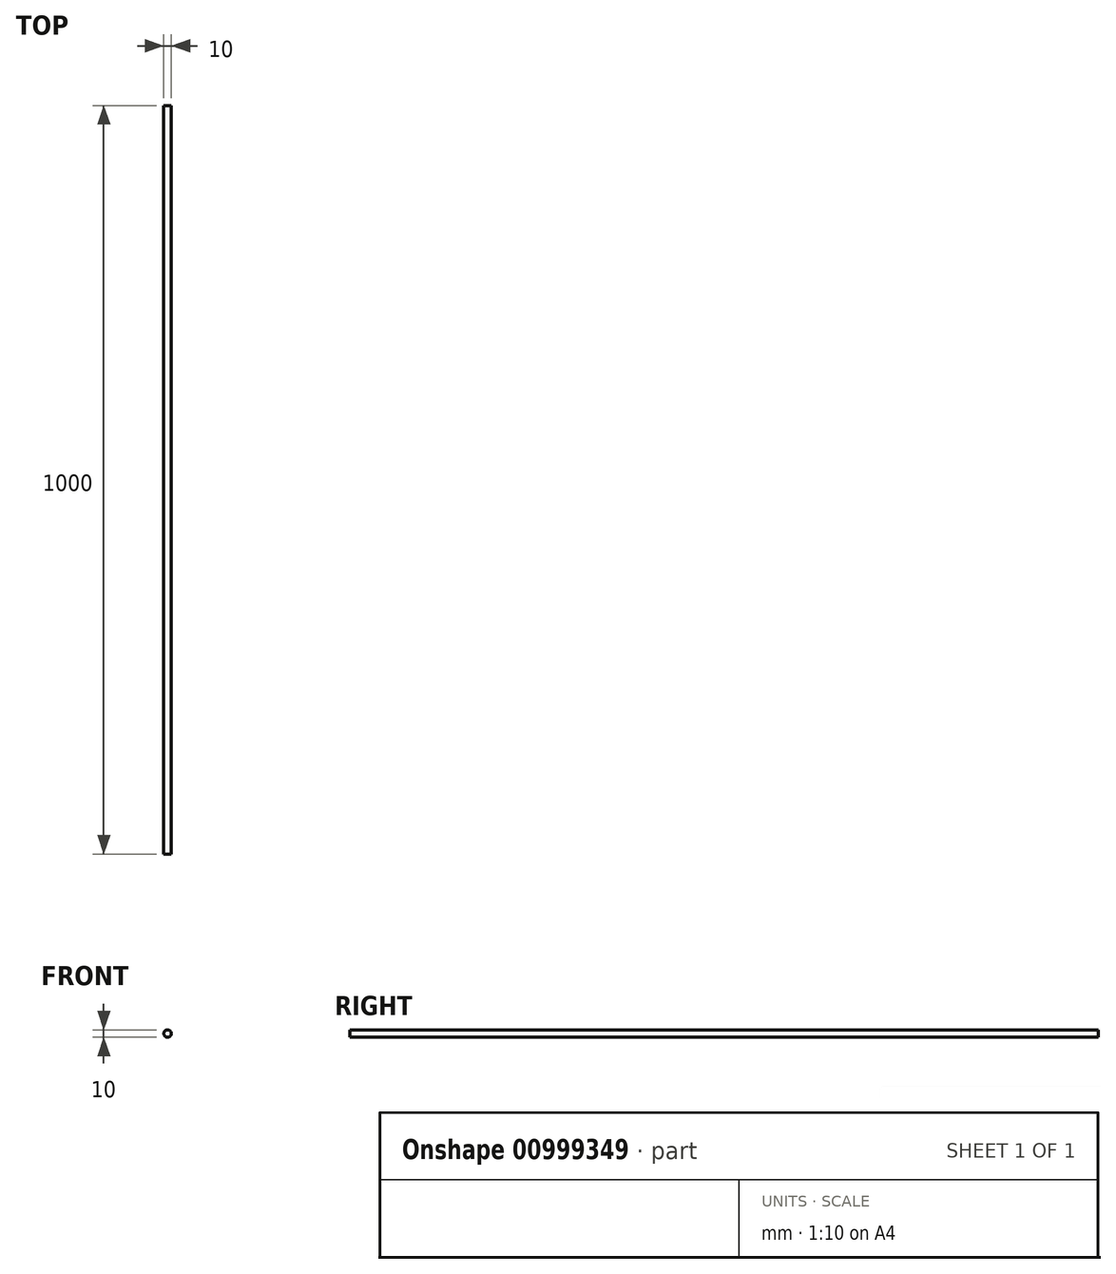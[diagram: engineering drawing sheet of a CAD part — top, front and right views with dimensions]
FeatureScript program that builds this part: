
annotation { "Feature Type Name" : "Feature", "Feature Type Description" : "" }
export const myFeature = defineFeature(function(context is Context, id is Id, definition is map)
    precondition{}
    {
        {
            var Q0;
            Q0=qCreatedBy(makeId("Front.planeOp"),FACE);
            var sketch = newSketch(context, id + "F0", { "sketchPlane" : qUnion([Q0])});
            skCircle(sketch, "E0", {"center": v(0, 0) * mm, "radius": 5 * mm});
            skSolve(sketch);
        }
        {
            var Q0;
            Q0=makeQuery(id+"F0.imprint","IMPRINT",FACE,{"disambiguationData":[TD([[makeQuery(id+"F0.imprint","IMPRINT",EDGE,{"derivedFrom":sQuery(id+"F0.wireOp",EDGE,"E0")}),1.0]])]});
            extrude(context, id + "F1", {"entities" : qUnion([Q0]), "depth" : 1000 * mm, "offsetDistance" : 25 * mm, "symmetric" : true});
        }
    });
